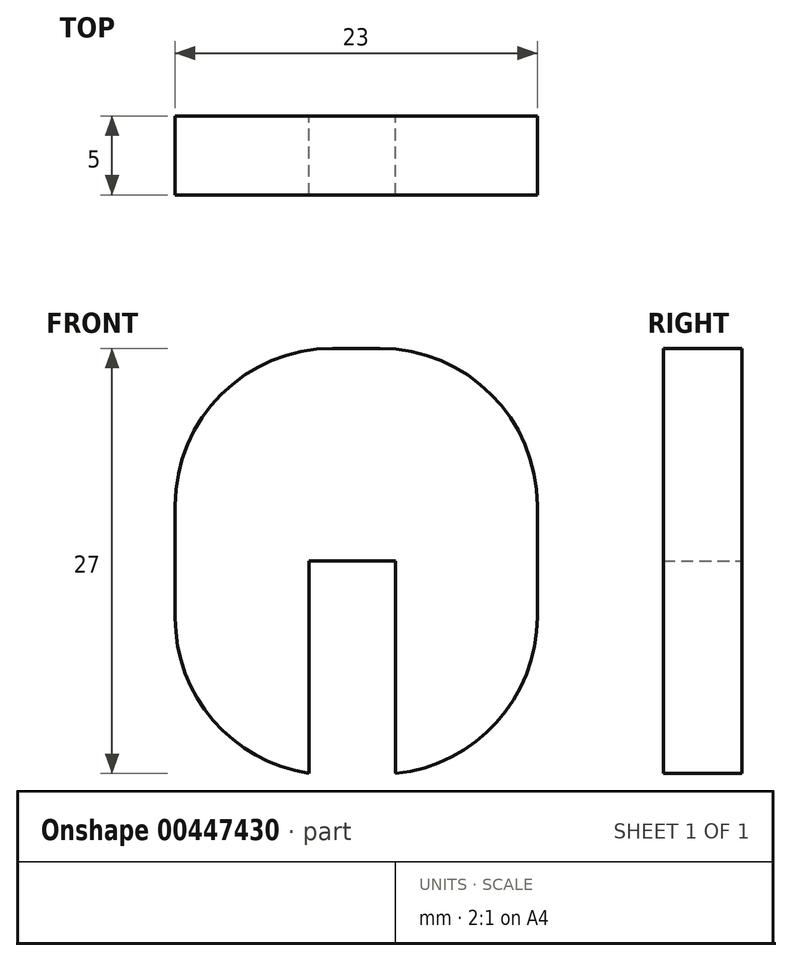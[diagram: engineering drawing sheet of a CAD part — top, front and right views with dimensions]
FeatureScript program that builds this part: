
annotation { "Feature Type Name" : "Feature", "Feature Type Description" : "" }
export const myFeature = defineFeature(function(context is Context, id is Id, definition is map)
    precondition{}
    {
        {
            var Q0;
            Q0=qCreatedBy(makeId("Front.planeOp"),FACE);
            var sketch = newSketch(context, id + "F0", { "sketchPlane" : qUnion([Q0])});
            skLineSegment(sketch, "E0.bottom", {"start": v(11.5, -13.5) * mm, "end": v(-11.5, -13.5) * mm});
            skLineSegment(sketch, "E0.top", {"start": v(11.5, 13.5) * mm, "end": v(-11.5, 13.5) * mm});
            skLineSegment(sketch, "E0.left", {"start": v(11.5, -13.5) * mm, "end": v(11.5, 13.5) * mm});
            skLineSegment(sketch, "E0.right", {"start": v(-11.5, -13.5) * mm, "end": v(-11.5, 13.5) * mm});
            skPoint(sketch, "E0.middle", {"position": v(0, 0) * mm});
            skLineSegment(sketch, "E1.bottom", {"start": v(-3, -13.5) * mm, "end": v(2.5, -13.5) * mm});
            skLineSegment(sketch, "E1.top", {"start": v(-3, 0) * mm, "end": v(2.5, 0) * mm});
            skLineSegment(sketch, "E1.left", {"start": v(-3, -13.5) * mm, "end": v(-3, 0) * mm});
            skLineSegment(sketch, "E1.right", {"start": v(2.5, -13.5) * mm, "end": v(2.5, 0) * mm});
            skSolve(sketch);
        }
        {
            var Q0;
            Q0=makeQuery(id+"F0.imprint","IMPRINT",FACE,{"disambiguationData":[TD([[makeQuery(id+"F0.imprint","IMPRINT",EDGE,{"derivedFrom":sQuery(id+"F0.wireOp",EDGE,"E0.top")}),1.0]])]});
            extrude(context, id + "F1", {"entities" : qUnion([Q0]), "depth" : 5 * mm});
        }
        {
            var Q0;
            Q0=makeQuery(id+"F1.opExtrude","SWEPT_EDGE",EDGE,{"disambiguationData":[OSD([sQuery(id+"F0.wireOp",EDGE,"E0.top"),sQuery(id+"F0.wireOp",EDGE,"E0.right")])]});
            var Q1;
            Q1=makeQuery(id+"F1.opExtrude","SWEPT_EDGE",EDGE,{"disambiguationData":[OSD([sQuery(id+"F0.wireOp",EDGE,"E0.top"),sQuery(id+"F0.wireOp",EDGE,"E0.left")])]});
            var Q2;
            Q2=makeQuery(id+"F1.opExtrude","SWEPT_EDGE",EDGE,{"disambiguationData":[OSD([sQuery(id+"F0.wireOp",EDGE,"E0.bottom"),sQuery(id+"F0.wireOp",EDGE,"E0.left")])]});
            var Q3;
            Q3=makeQuery(id+"F1.opExtrude","SWEPT_EDGE",EDGE,{"disambiguationData":[OSD([sQuery(id+"F0.wireOp",EDGE,"E0.bottom"),sQuery(id+"F0.wireOp",EDGE,"E0.right")])]});
            fillet(context, id + "F2", {"entities" : qUnion([Q0, Q1, Q2, Q3]), "radius" : 10 * mm, "tangentPropagation" : true, "allowEdgeOverflow" : false});
        }
    });
